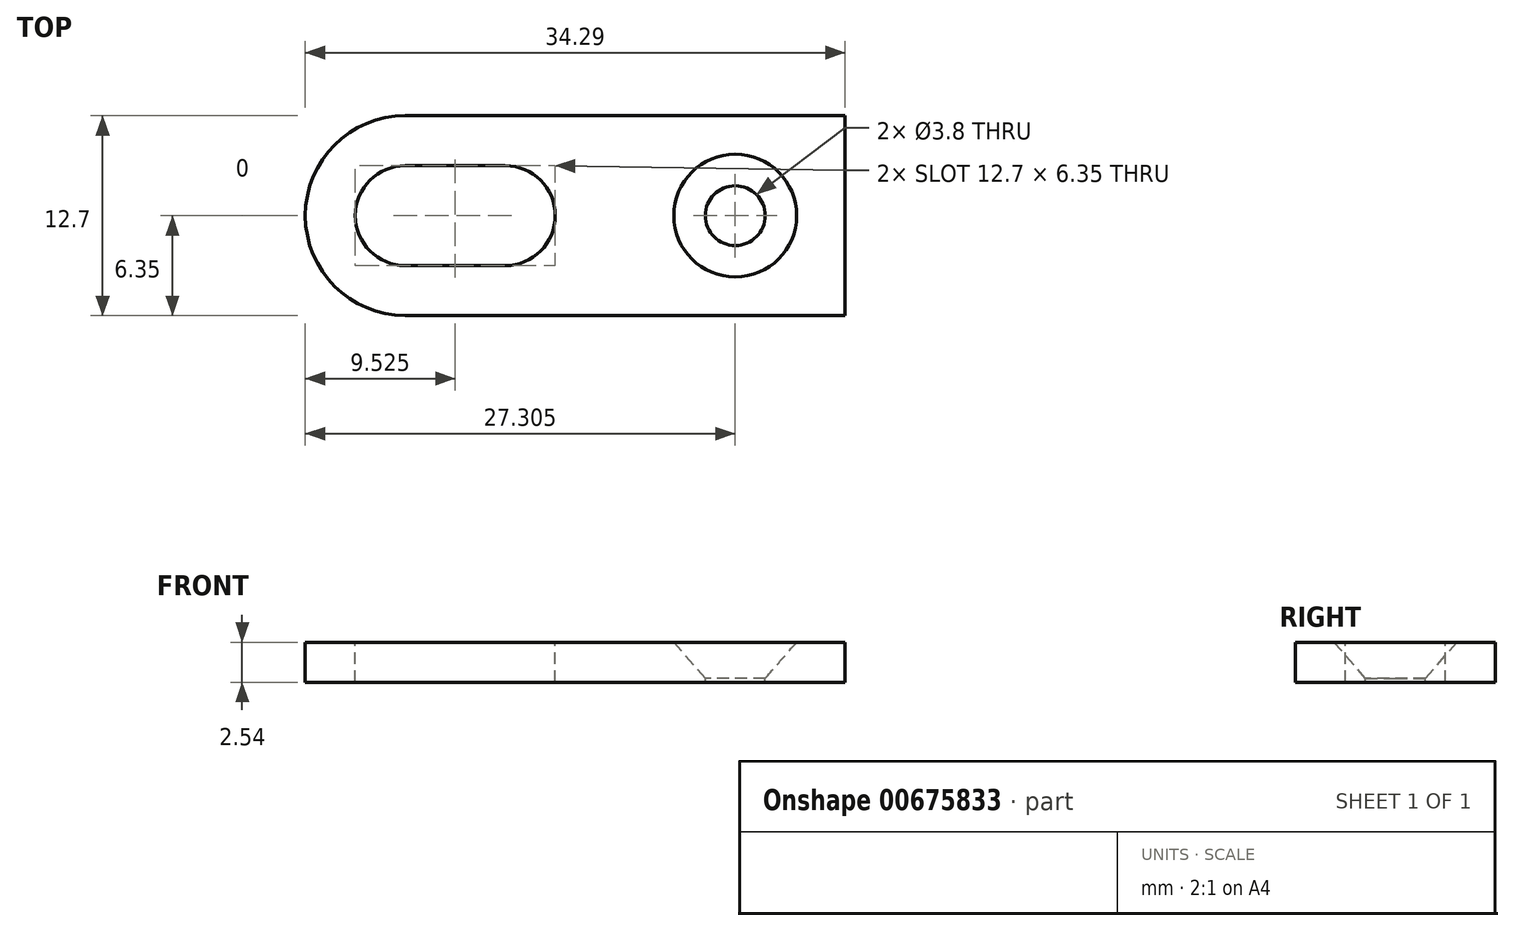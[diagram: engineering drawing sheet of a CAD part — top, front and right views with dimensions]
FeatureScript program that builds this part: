
annotation { "Feature Type Name" : "Feature", "Feature Type Description" : "" }
export const myFeature = defineFeature(function(context is Context, id is Id, definition is map)
    precondition{}
    {
        {
            var Q0;
            Q0=qCreatedBy(makeId("Top.planeOp"),FACE);
            var sketch = newSketch(context, id + "F0", { "sketchPlane" : qUnion([Q0])});
            skLineSegment(sketch, "E0.bottom", {"start": v(6.35, 0) * mm, "end": v(34.3, 0) * mm});
            skLineSegment(sketch, "E0.top", {"start": v(6.35, 12.7) * mm, "end": v(34.3, 12.7) * mm});
            skLineSegment(sketch, "E0.left", {"start": v(0, 6.35) * mm, "end": v(0, 6.35) * mm});
            skLineSegment(sketch, "E0.right", {"start": v(34.3, 0) * mm, "end": v(34.3, 12.7) * mm});
            skPoint(sketch, "E1.visualSharp", {"position": v(0, 12.7) * mm});
            skArc(sketch, "E1.filletArc", {"start": v(6.35, 12.7) * mm, "mid": v(1.86, 10.84) * mm, "end": v(0, 6.35) * mm});
            skPoint(sketch, "E2.visualSharp", {"position": v(0, 0) * mm});
            skArc(sketch, "E2.filletArc", {"start": v(0, 6.35) * mm, "mid": v(1.86, 1.86) * mm, "end": v(6.35, 0) * mm});
            skPoint(sketch, "E3.visualSharp", {"position": v(34.3, 12.7) * mm});
            skSolve(sketch);
        }
        {
            var Q0;
            Q0 = qSketchRegion(id + "F0", true);
            extrude(context, id + "F1", {"entities" : qUnion([Q0]), "depth" : 2.54 * mm, "offsetDistance" : 25.4 * mm});
        }
        {
            var Q0;
            Q0=makeQuery(id+"F1.opExtrude","CAP_FACE",FACE,{"disambiguationData":[OSD([sQuery(id+"F0.wireOp",EDGE,"E0.bottom"),sQuery(id+"F0.wireOp",EDGE,"E0.top"),sQuery(id+"F0.wireOp",EDGE,"E0.left"),sQuery(id+"F0.wireOp",EDGE,"E0.right")])],"isStart":false});
            var sketch = newSketch(context, id + "F2", { "sketchPlane" : qUnion([Q0])});
            skArc(sketch, "E4", {"start": v(6.35, 9.53) * mm, "mid": v(3.17, 6.35) * mm, "end": v(6.35, 3.18) * mm});
            skLineSegment(sketch, "E5", {"start": v(0, 6.35) * mm, "end": v(34.3, 6.35) * mm, "construction": true});
            skArc(sketch, "E6", {"start": v(12.7, 3.18) * mm, "mid": v(15.87, 6.35) * mm, "end": v(12.7, 9.53) * mm});
            skLineSegment(sketch, "E7", {"start": v(6.35, 9.53) * mm, "end": v(12.7, 9.53) * mm});
            skLineSegment(sketch, "E8", {"start": v(12.7, 3.18) * mm, "end": v(6.35, 3.18) * mm});
            skSolve(sketch);
        }
        {
            var Q0;
            Q0 = qSketchRegion(id + "F2", true);
            extrude(context, id + "F3", {"entities" : qUnion([Q0]), "operationType" : NewBodyOperationType.REMOVE, "endBound" : BoundingType.THROUGH_ALL, "oppositeDirection" : true, "depth" : 25.4 * mm, "offsetDistance" : 25.4 * mm});
        }
        {
            var Q0;
            Q0=makeQuery(id+"F1.opExtrude","CAP_FACE",FACE,{"disambiguationData":[OSD([sQuery(id+"F0.wireOp",EDGE,"E0.bottom"),sQuery(id+"F0.wireOp",EDGE,"E0.top"),sQuery(id+"F0.wireOp",EDGE,"E0.left"),sQuery(id+"F0.wireOp",EDGE,"E0.right")])],"isStart":false});
            var sketch = newSketch(context, id + "F4", { "sketchPlane" : qUnion([Q0])});
            skPoint(sketch, "E9", {"position": v(27.3, 6.35) * mm});
            skLineSegment(sketch, "E10", {"start": v(0, 6.35) * mm, "end": v(34.3, 6.35) * mm, "construction": true});
            skLineSegment(sketch, "E11", {"start": v(9.53, 9.52) * mm, "end": v(9.53, 3.17) * mm, "construction": true});
            skSolve(sketch);
        }
        {
            var Q0;
            Q0=sQuery(id+"F4.wireOp",VERTEX,"E9");
            var Q1;
            Q1=makeQuery(id+"F1.opExtrude","SWEPT_BODY",BODY,{"disambiguationData":[OSD([sQuery(id+"F0.wireOp",EDGE,"E0.bottom"),sQuery(id+"F0.wireOp",EDGE,"E0.top"),sQuery(id+"F0.wireOp",EDGE,"E0.left"),sQuery(id+"F0.wireOp",EDGE,"E0.right")])]});
            hole(context, id + "F5", {"style" : HoleStyle.C_SINK, "endStyle" : HoleEndStyle.THROUGH, "standardTappedOrClearance" : lookupTablePath({ "standard" : "ANSI", "fit" : "Normal (ASME)", "size" : "#6", "type" : "Clearance" }), "standardBlindInLast" : lookupTablePath({ "fit" : "Free", "standard" : "ANSI", "size" : "#6", "type" : "Clearance" }), "holeDiameter" : 3.8 * mm, "cSinkDiameter" : 7.8 * mm, "cSinkAngle" : 82 * degree, "majorDiameter" : 3.5 * mm, "isTappedThrough" : true, "tappedDepth" : 10.32 * mm, "tapClearance" : 3, "startFromSketch" : true, "locations" : qUnion([Q0]), "scope" : qUnion([Q1])});
        }
    });
